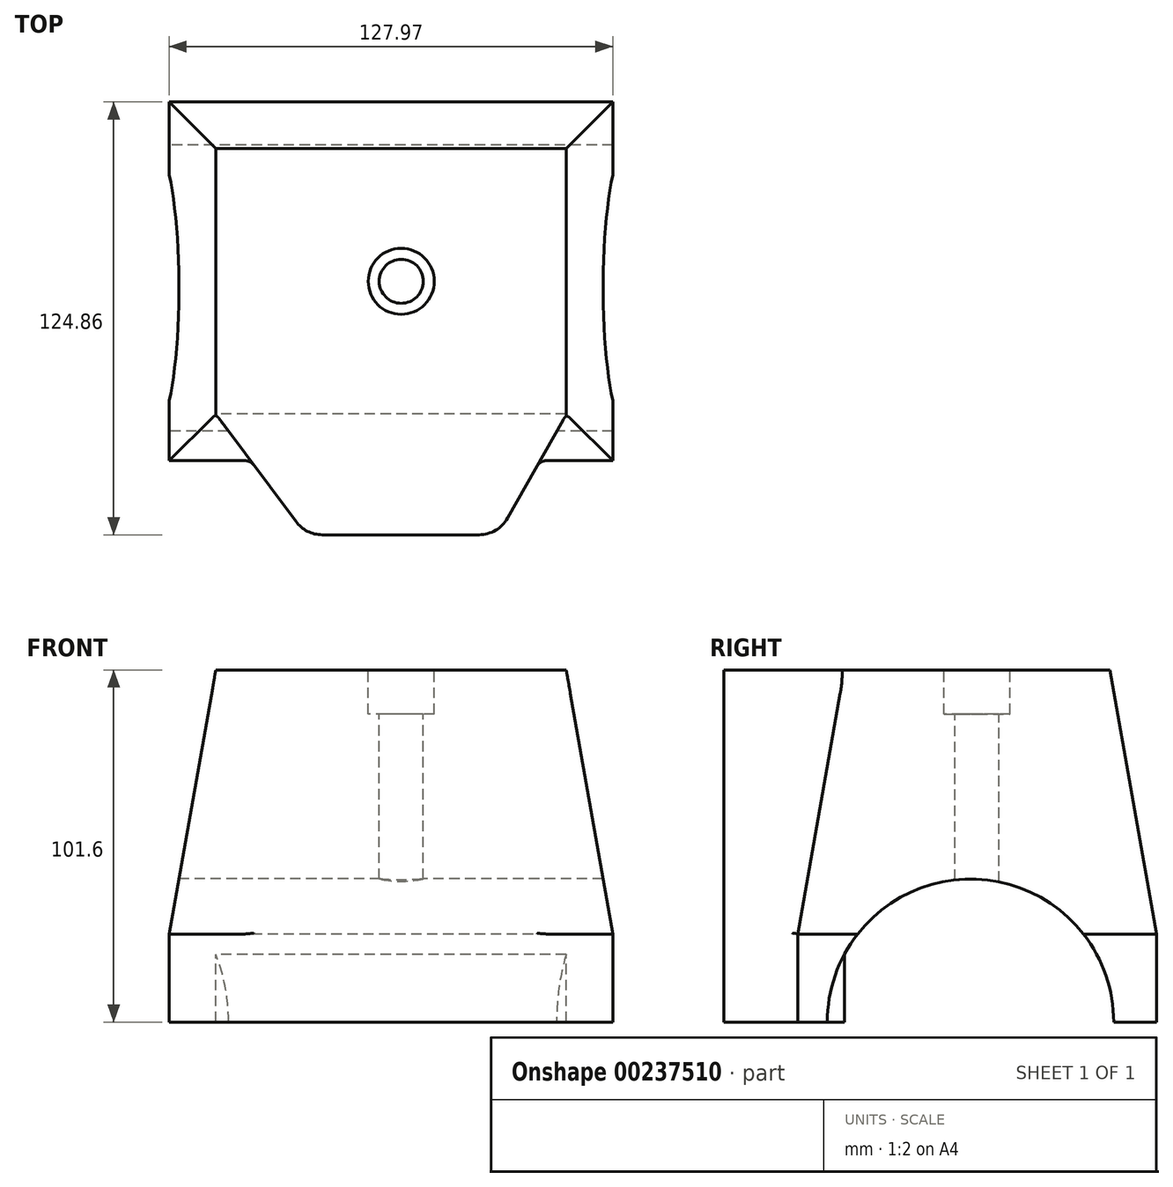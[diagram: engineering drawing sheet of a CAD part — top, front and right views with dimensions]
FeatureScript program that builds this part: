
annotation { "Feature Type Name" : "Feature", "Feature Type Description" : "" }
export const myFeature = defineFeature(function(context is Context, id is Id, definition is map)
    precondition{}
    {
        {
            var Q0;
            Q0=qCreatedBy(makeId("Top.planeOp"),FACE);
            var sketch = newSketch(context, id + "F0", { "sketchPlane" : qUnion([Q0])});
            skLineSegment(sketch, "E0.bottom", {"start": v(61.03, 51.73) * mm, "end": v(-66.94, 51.73) * mm});
            skLineSegment(sketch, "E0.top", {"start": v(61.03, -51.75) * mm, "end": v(-66.94, -51.75) * mm});
            skLineSegment(sketch, "E0.left", {"start": v(61.03, 51.73) * mm, "end": v(61.03, -51.75) * mm});
            skLineSegment(sketch, "E0.right", {"start": v(-66.94, 51.73) * mm, "end": v(-66.94, -51.75) * mm});
            skSolve(sketch);
        }
        {
            var Q0;
            Q0 = qSketchRegion(id + "F0", true);
            extrude(context, id + "F1", {"entities" : qUnion([Q0]), "depth" : 25.4 * mm});
        }
        {
            var Q0;
            Q0=makeQuery(id+"F1.opExtrude","CAP_FACE",FACE,{"disambiguationData":[OSD([sQuery(id+"F0.wireOp",EDGE,"E0.bottom"),sQuery(id+"F0.wireOp",EDGE,"E0.top"),sQuery(id+"F0.wireOp",EDGE,"E0.left"),sQuery(id+"F0.wireOp",EDGE,"E0.right")])],"isStart":false});
            var Q1;
            Q1=makeQuery(id+"F1.opExtrude","CAP_FACE",FACE,{"disambiguationData":[OSD([sQuery(id+"F0.wireOp",EDGE,"E0.bottom"),sQuery(id+"F0.wireOp",EDGE,"E0.top"),sQuery(id+"F0.wireOp",EDGE,"E0.left"),sQuery(id+"F0.wireOp",EDGE,"E0.right")])],"isStart":true});
            extrude(context, id + "F2", {"entities" : qUnion([Q0, Q1]), "operationType" : NewBodyOperationType.ADD, "depth" : 76.2 * mm, "hasDraft" : true, "draftAngle" : 10 * degree, "draftPullDirection" : true});
        }
        {
            var Q0;
            Q0=qCreatedBy(makeId("Right.planeOp"),FACE);
            var sketch = newSketch(context, id + "F3", { "sketchPlane" : qUnion([Q0])});
            skCircle(sketch, "E1", {"center": v(-1.93, 0) * mm, "radius": 41.32 * mm});
            skSolve(sketch);
        }
        {
            var Q0;
            Q0 = qSketchRegion(id + "F3", true);
            extrude(context, id + "F4", {"entities" : qUnion([Q0]), "operationType" : NewBodyOperationType.REMOVE, "endBound" : BoundingType.SYMMETRIC, "depth" : 152.4 * mm});
        }
        {
            var Q0;
            {var subQ0=sQuery(id+"F0.wireOp",EDGE,"E0.right");var subQ1=sQuery(id+"F0.wireOp",EDGE,"E0.left");var subQ2=sQuery(id+"F0.wireOp",EDGE,"E0.top");var subQ3=sQuery(id+"F0.wireOp",EDGE,"E0.bottom");Q0=makeQuery(id+"F2.opExtrude","CAP_FACE",FACE,{"disambiguationData":[OSD([subQ3,subQ2,subQ1,subQ0]),TDD([makeQuery(id+"F1.opExtrude","CAP_FACE",FACE,{"disambiguationData":[OSD([subQ3,subQ2,subQ1,subQ0])],"isStart":false})])],"isStart":false});}
            var sketch = newSketch(context, id + "F5", { "sketchPlane" : qUnion([Q0])});
            skCircle(sketch, "E2", {"center": v(0, 0) * mm, "radius": 16.3 * mm});
            skSolve(sketch);
        }
        {
            var Q0;
            Q0=sQuery(id+"F5.wireOp",VERTEX,"E2.center");
            var Q1;
            Q1=makeQuery(id+"F1.opExtrude","SWEPT_BODY",BODY,{"disambiguationData":[OSD([sQuery(id+"F0.wireOp",EDGE,"E0.bottom"),sQuery(id+"F0.wireOp",EDGE,"E0.top"),sQuery(id+"F0.wireOp",EDGE,"E0.left"),sQuery(id+"F0.wireOp",EDGE,"E0.right")])]});
            hole(context, id + "F6", {"style" : HoleStyle.C_BORE, "endStyle" : HoleEndStyle.THROUGH, "holeDiameter" : 12.7 * mm, "cBoreDiameter" : 19.05 * mm, "cBoreDepth" : 12.7 * mm, "startFromSketch" : true, "locations" : qUnion([Q0]), "scope" : qUnion([Q1]), "isTappedThrough" : true});
        }
        {
            var Q0;
            {var subQ0=sQuery(id+"F0.wireOp",EDGE,"E0.right");var subQ1=sQuery(id+"F0.wireOp",EDGE,"E0.left");var subQ2=sQuery(id+"F0.wireOp",EDGE,"E0.top");var subQ3=sQuery(id+"F0.wireOp",EDGE,"E0.bottom");Q0=makeQuery(id+"F2.opExtrude","CAP_FACE",FACE,{"disambiguationData":[OSD([subQ3,subQ2,subQ1,subQ0]),TDD([makeQuery(id+"F1.opExtrude","CAP_FACE",FACE,{"disambiguationData":[OSD([subQ3,subQ2,subQ1,subQ0])],"isStart":false})])],"isStart":false});}
            var sketch = newSketch(context, id + "F7", { "sketchPlane" : qUnion([Q0])});
            skLineSegment(sketch, "E3", {"start": v(-53.5, -38.32) * mm, "end": v(-30.4, -69.3) * mm});
            skLineSegment(sketch, "E4", {"start": v(-22.77, -73.13) * mm, "end": v(22.42, -73.13) * mm});
            skLineSegment(sketch, "E5", {"start": v(30.71, -68.29) * mm, "end": v(47.6, -38.32) * mm});
            skPoint(sketch, "E6.visualSharp", {"position": v(-27.55, -73.13) * mm});
            skArc(sketch, "E6.filletArc", {"start": v(-30.4, -69.3) * mm, "mid": v(-27.04, -72.12) * mm, "end": v(-22.77, -73.13) * mm});
            skPoint(sketch, "E7.visualSharp", {"position": v(27.98, -73.13) * mm});
            skArc(sketch, "E7.filletArc", {"start": v(22.42, -73.13) * mm, "mid": v(27.22, -71.83) * mm, "end": v(30.71, -68.29) * mm});
            skSolve(sketch);
        }
        {
            var Q0;
            Q0=makeQuery(id+"F7.imprint","IMPRINT",FACE,{"disambiguationData":[TD([[makeQuery(id+"F7.imprint","IMPRINT",EDGE,{"derivedFrom":sQuery(id+"F7.wireOp",EDGE,"E3")}),1.0]])]});
            extrude(context, id + "F8", {"entities" : qUnion([Q0]), "operationType" : NewBodyOperationType.ADD, "oppositeDirection" : true, "depth" : 101.6 * mm});
        }
        {
            var Q0;
            {var subQ0=sQuery(id+"F0.wireOp",EDGE,"E0.top");Q0=makeQuery(id+"F8.boolean.opBoolean","INTERSECT",EDGE,{"derivedFrom":[makeQuery(id+"F2.opExtrude","SWEPT_FACE",FACE,{"disambiguationData":[OSD([subQ0]),TDD([makeQuery(id+"F1.opExtrude","CAP_EDGE",EDGE,{"disambiguationData":[OSD([subQ0])],"isStart":false})])]}),makeQuery(id+"F8.opExtrude","SWEPT_FACE",FACE,{"disambiguationData":[OSD([sQuery(id+"F7.wireOp",EDGE,"E5")])]})]});}
            var Q1;
            Q1=makeQuery(id+"F8.boolean.opBoolean","INTERSECT",EDGE,{"derivedFrom":[makeQuery(id+"F1.opExtrude","SWEPT_FACE",FACE,{"disambiguationData":[OSD([sQuery(id+"F0.wireOp",EDGE,"E0.top")])]}),makeQuery(id+"F8.opExtrude","SWEPT_FACE",FACE,{"disambiguationData":[OSD([sQuery(id+"F7.wireOp",EDGE,"E5")])]})]});
            fillet(context, id + "F9", {"entities" : qUnion([Q0, Q1]), "radius" : 3.17 * mm, "tangentPropagation" : true, "allowEdgeOverflow" : false});
        }
        {
            var Q0;
            {var subQ0=sQuery(id+"F0.wireOp",EDGE,"E0.top");Q0=makeQuery(id+"F8.boolean.opBoolean","INTERSECT",EDGE,{"derivedFrom":[makeQuery(id+"F2.opExtrude","SWEPT_FACE",FACE,{"disambiguationData":[OSD([subQ0]),TDD([makeQuery(id+"F1.opExtrude","CAP_EDGE",EDGE,{"disambiguationData":[OSD([subQ0])],"isStart":false})])]}),makeQuery(id+"F8.opExtrude","SWEPT_FACE",FACE,{"disambiguationData":[OSD([sQuery(id+"F7.wireOp",EDGE,"E3")])]})]});}
            var Q1;
            Q1=makeQuery(id+"F8.boolean.opBoolean","INTERSECT",EDGE,{"derivedFrom":[makeQuery(id+"F1.opExtrude","SWEPT_FACE",FACE,{"disambiguationData":[OSD([sQuery(id+"F0.wireOp",EDGE,"E0.top")])]}),makeQuery(id+"F8.opExtrude","SWEPT_FACE",FACE,{"disambiguationData":[OSD([sQuery(id+"F7.wireOp",EDGE,"E3")])]})]});
            fillet(context, id + "F10", {"entities" : qUnion([Q0, Q1]), "radius" : 3.17 * mm, "tangentPropagation" : true, "allowEdgeOverflow" : false});
        }
    });
